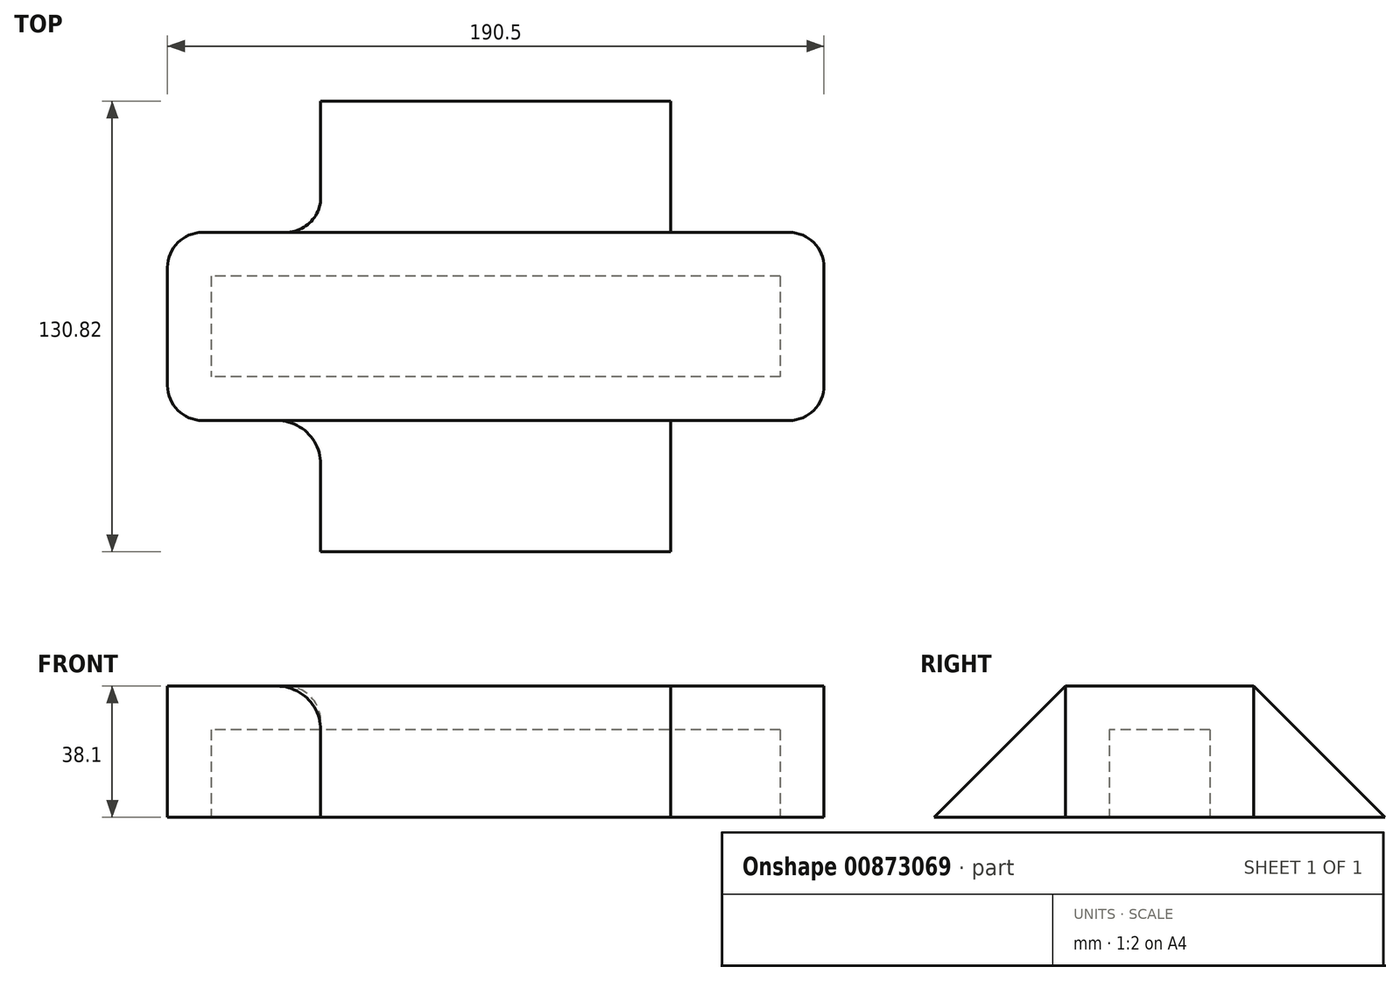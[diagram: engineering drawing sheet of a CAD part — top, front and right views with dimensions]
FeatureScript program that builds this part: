
annotation { "Feature Type Name" : "Feature", "Feature Type Description" : "" }
export const myFeature = defineFeature(function(context is Context, id is Id, definition is map)
    precondition{}
    {
        {
            var Q0;
            Q0=qCreatedBy(makeId("Top.planeOp"),FACE);
            var sketch = newSketch(context, id + "F0", { "sketchPlane" : qUnion([Q0])});
            skLineSegment(sketch, "E0.bottom", {"start": v(95.25, -27.3) * mm, "end": v(-95.25, -27.3) * mm});
            skLineSegment(sketch, "E0.top", {"start": v(95.25, 27.3) * mm, "end": v(-95.25, 27.3) * mm});
            skLineSegment(sketch, "E0.left", {"start": v(95.25, -27.3) * mm, "end": v(95.25, 27.3) * mm});
            skLineSegment(sketch, "E0.right", {"start": v(-95.25, -27.3) * mm, "end": v(-95.25, 27.3) * mm});
            skPoint(sketch, "E0.middle", {"position": v(0, 0) * mm});
            skSolve(sketch);
        }
        {
            var Q0;
            Q0 = qSketchRegion(id + "F0", true);
            extrude(context, id + "F1", {"entities" : qUnion([Q0]), "depth" : 38.1 * mm, "offsetDistance" : 25.4 * mm});
        }
        {
            var Q0;
            Q0=makeQuery(id+"F1.opExtrude","CAP_FACE",FACE,{"disambiguationData":[OSD([sQuery(id+"F0.wireOp",EDGE,"E0.bottom"),sQuery(id+"F0.wireOp",EDGE,"E0.top"),sQuery(id+"F0.wireOp",EDGE,"E0.left"),sQuery(id+"F0.wireOp",EDGE,"E0.right")])],"isStart":true});
            var sketch = newSketch(context, id + "F2", { "sketchPlane" : qUnion([Q0])});
            skLineSegment(sketch, "E1.bottom", {"start": v(82.55, -14.6) * mm, "end": v(-82.55, -14.6) * mm});
            skLineSegment(sketch, "E1.top", {"start": v(82.55, 14.6) * mm, "end": v(-82.55, 14.6) * mm});
            skLineSegment(sketch, "E1.left", {"start": v(82.55, -14.6) * mm, "end": v(82.55, 14.6) * mm});
            skLineSegment(sketch, "E1.right", {"start": v(-82.55, -14.6) * mm, "end": v(-82.55, 14.6) * mm});
            skPoint(sketch, "E1.middle", {"position": v(0, 0) * mm});
            skSolve(sketch);
        }
        {
            var Q0;
            Q0 = qSketchRegion(id + "F2", true);
            extrude(context, id + "F3", {"entities" : qUnion([Q0]), "operationType" : NewBodyOperationType.REMOVE, "oppositeDirection" : true, "depth" : 25.4 * mm, "offsetDistance" : 25.4 * mm});
        }
        {
            var Q0;
            Q0=makeQuery(id+"F1.opExtrude","SWEPT_FACE",FACE,{"disambiguationData":[OSD([sQuery(id+"F0.wireOp",EDGE,"E0.top")])]});
            var sketch = newSketch(context, id + "F4", { "sketchPlane" : qUnion([Q0])});
            skLineSegment(sketch, "E2.bottom", {"start": v(50.8, 0) * mm, "end": v(-50.8, 0) * mm});
            skLineSegment(sketch, "E2.top", {"start": v(50.8, 38.1) * mm, "end": v(-50.8, 38.1) * mm});
            skLineSegment(sketch, "E2.left", {"start": v(50.8, 0) * mm, "end": v(50.8, 38.1) * mm});
            skLineSegment(sketch, "E2.right", {"start": v(-50.8, 0) * mm, "end": v(-50.8, 38.1) * mm});
            skPoint(sketch, "E2.middle", {"position": v(0, 19.05) * mm});
            skPoint(sketch, "E2.middle.positionSnap0", {"position": v(95.25, 19.05) * mm});
            skPoint(sketch, "E2.middle.positionSnap1", {"position": v(0, 0) * mm});
            skPoint(sketch, "E2.centerSnap0", {"position": v(95.25, 19.05) * mm});
            skPoint(sketch, "E2.centerSnap1", {"position": v(0, 0) * mm});
            skSolve(sketch);
        }
        {
            var Q0;
            Q0=makeQuery(id+"F4.imprint","IMPRINT",FACE,{"disambiguationData":[TD([[makeQuery(id+"F4.imprint","IMPRINT",EDGE,{"derivedFrom":sQuery(id+"F4.wireOp",EDGE,"E2.bottom")}),1.0]])]});
            extrude(context, id + "F5", {"entities" : qUnion([Q0]), "operationType" : NewBodyOperationType.ADD, "depth" : 38.1 * mm, "offsetDistance" : 25.4 * mm});
        }
        {
            var Q0;
            Q0=makeQuery(id+"F5.opExtrude","CAP_EDGE",EDGE,{"disambiguationData":[OSD([sQuery(id+"F4.wireOp",EDGE,"E2.top")])],"isStart":false});
            chamfer(context, id + "F6", {"entities" : qUnion([Q0]), "width" : 38.1 * mm, "tangentPropagation" : true});
        }
        {
            var Q0;
            Q0=makeQuery(id+"F5.opExtrude","CAP_EDGE",EDGE,{"disambiguationData":[OSD([sQuery(id+"F4.wireOp",EDGE,"E2.left")])],"isStart":true});
            var Q1;
            Q1=makeQuery(id+"F5.opExtrude","CAP_EDGE",EDGE,{"disambiguationData":[OSD([sQuery(id+"F4.wireOp",EDGE,"E2.right")])],"isStart":true});
            fillet(context, id + "F7", {"entities" : qUnion([Q0, Q1]), "radius" : 10.16 * mm, "tangentPropagation" : true, "allowEdgeOverflow" : false});
        }
        {
            var Q0;
            Q0=makeQuery(id+"F1.opExtrude","SWEPT_EDGE",EDGE,{"disambiguationData":[OSD([sQuery(id+"F0.wireOp",EDGE,"E0.top"),sQuery(id+"F0.wireOp",EDGE,"E0.right")])]});
            var Q1;
            Q1=makeQuery(id+"F1.opExtrude","SWEPT_EDGE",EDGE,{"disambiguationData":[OSD([sQuery(id+"F0.wireOp",EDGE,"E0.bottom"),sQuery(id+"F0.wireOp",EDGE,"E0.right")])]});
            var Q2;
            Q2=makeQuery(id+"F1.opExtrude","SWEPT_EDGE",EDGE,{"disambiguationData":[OSD([sQuery(id+"F0.wireOp",EDGE,"E0.top"),sQuery(id+"F0.wireOp",EDGE,"E0.left")])]});
            var Q3;
            Q3=makeQuery(id+"F1.opExtrude","SWEPT_EDGE",EDGE,{"disambiguationData":[OSD([sQuery(id+"F0.wireOp",EDGE,"E0.bottom"),sQuery(id+"F0.wireOp",EDGE,"E0.left")])]});
            fillet(context, id + "F8", {"entities" : qUnion([Q0, Q1, Q2, Q3]), "radius" : 10.16 * mm, "tangentPropagation" : true, "allowEdgeOverflow" : false});
        }
        {
            var Q0;
            Q0=makeQuery(id+"F1.opExtrude","SWEPT_FACE",FACE,{"disambiguationData":[OSD([sQuery(id+"F0.wireOp",EDGE,"E0.bottom")])]});
            var sketch = newSketch(context, id + "F9", { "sketchPlane" : qUnion([Q0])});
            skLineSegment(sketch, "E3.bottom", {"start": v(50.8, 0) * mm, "end": v(-50.8, 0) * mm});
            skLineSegment(sketch, "E3.top", {"start": v(50.8, 38.1) * mm, "end": v(-50.8, 38.1) * mm});
            skLineSegment(sketch, "E3.left", {"start": v(50.8, 0) * mm, "end": v(50.8, 38.1) * mm});
            skLineSegment(sketch, "E3.right", {"start": v(-50.8, 0) * mm, "end": v(-50.8, 38.1) * mm});
            skPoint(sketch, "E3.middle", {"position": v(0, 19.05) * mm});
            skPoint(sketch, "E3.middle.positionSnap0", {"position": v(0, 0) * mm});
            skPoint(sketch, "E3.middle.positionSnap1", {"position": v(-85.1, 19.05) * mm});
            skPoint(sketch, "E3.centerSnap0", {"position": v(0, 0) * mm});
            skPoint(sketch, "E3.centerSnap1", {"position": v(-85.1, 19.05) * mm});
            skSolve(sketch);
        }
        {
            var Q0;
            Q0 = qSketchRegion(id + "F9", true);
            extrude(context, id + "F10", {"entities" : qUnion([Q0]), "operationType" : NewBodyOperationType.ADD, "depth" : 38.1 * mm, "offsetDistance" : 25.4 * mm});
        }
        {
            var Q0;
            Q0=makeQuery(id+"F10.opExtrude","CAP_EDGE",EDGE,{"disambiguationData":[OSD([sQuery(id+"F9.wireOp",EDGE,"E3.top")])],"isStart":false});
            chamfer(context, id + "F11", {"entities" : qUnion([Q0]), "width" : 38.1 * mm, "tangentPropagation" : true});
        }
        {
            var Q0;
            Q0=makeQuery(id+"F10.opExtrude","CAP_EDGE",EDGE,{"disambiguationData":[OSD([sQuery(id+"F9.wireOp",EDGE,"E3.left")])],"isStart":true});
            var Q1;
            Q1=makeQuery(id+"F10.opExtrude","CAP_EDGE",EDGE,{"disambiguationData":[OSD([sQuery(id+"F9.wireOp",EDGE,"E3.right")])],"isStart":true});
            fillet(context, id + "F12", {"entities" : qUnion([Q0, Q1]), "radius" : 12.7 * mm, "tangentPropagation" : true, "allowEdgeOverflow" : false});
        }
    });
